# Revit family: 340021001_Sanitario Laguna
name_source: partatom
category: Plumbing Fixtures
units: mm (PartAtom-declared; Revit-internal decimal feet)

## family parameters
Always vertical = Yes
Cut with Voids When Loaded = No
OmniClass Number = 23.45.00.00
Part Type = Normal
Room Calculation Point = No
Round Connector Dimension = Use Diameter
Shared = No
Work Plane-Based = No

## types (1)
- 340021001_Sanitario Laguna
    A2 = 370 mm  [stored 1.21391 ft]
    Alto = 719 mm  [stored 2.35892 ft]
    Ancho = 389 mm  [stored 1.27625 ft]
    Años de Garantía = 5 años en Griferia
    Consumo de Agua = 4.8 Lpf. - 1.28 gpf
    Creado por = IDD
    Description = sanitario de estilo tradicional, con taza y tanque separados que puedes reemplazar por separado.
    Espejo de agua = 185 x 213 mm. - 7,3 x 8,4 pulg.
    Fecha de creación = 12/08/2020
    Manufacturer = Corona
    Material = Corona_Porcelana_Sanitaria
    Peso Bruto aprox = 26,1 kg. - 57,5 lbs.
    Peso Neto aprox = 24,6 kg. - 54,2 lbs
    Presion minima = 20 - 80 PSI
    Referencia = 340021001
    URL = https://corona.co
    h1 = 374 mm  [stored 1.22703 ft]

note: [stored X ft] marks values corroborated as IEEE doubles in the binary element streams (Revit-internal decimal feet)

## geometry (parser evidence)
native form markers: Sweep x6
no freeform markers — native parametric forms only
